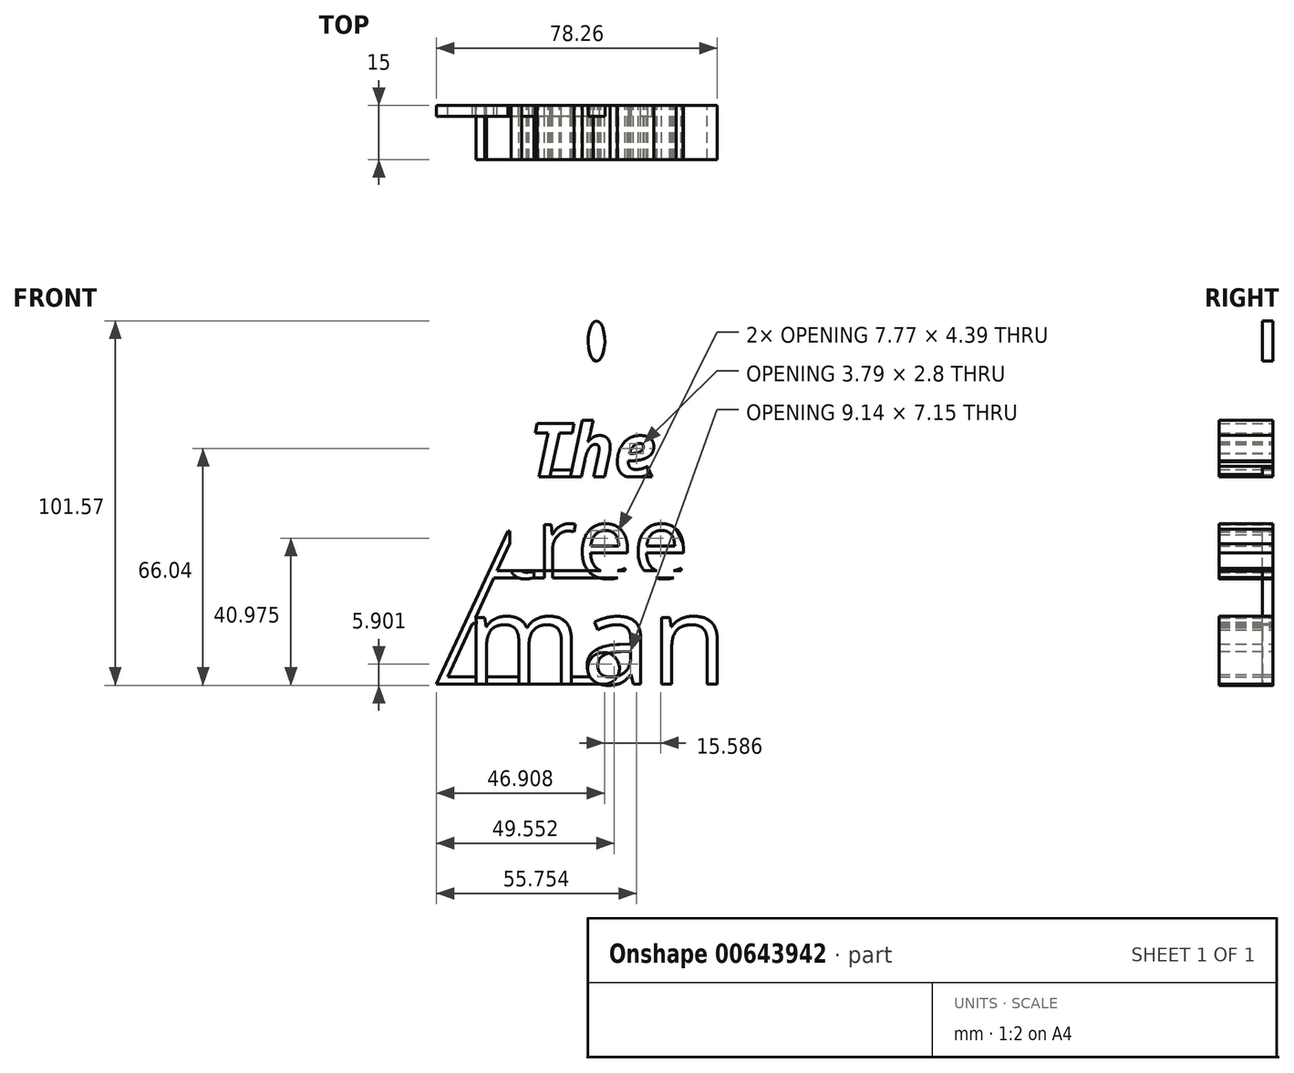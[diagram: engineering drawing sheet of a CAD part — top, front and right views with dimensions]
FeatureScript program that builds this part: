
annotation { "Feature Type Name" : "Feature", "Feature Type Description" : "" }
export const myFeature = defineFeature(function(context is Context, id is Id, definition is map)
    precondition{}
    {
        {
            var Q0;
            Q0=qCreatedBy(makeId("Front.planeOp"),FACE);
            var sketch = newSketch(context, id + "F0", { "sketchPlane" : qUnion([Q0])});
            skText(sketch, "E0", { "text": "The", "fontName": "OpenSans-BoldItalic.ttf"});
            skText(sketch, "E1", { "text": "tree", "fontName": "OpenSans-Regular.ttf"});
            skText(sketch, "E2", { "text": "man", "fontName": "OpenSans-Regular.ttf"});
            skLineSegment(sketch, "E3", {"start": v(-44.6, -34.27) * mm, "end": v(-24.68, 8.45) * mm});
            skLineSegment(sketch, "E4", {"start": v(0, 61.37) * mm, "end": v(12.27, 35.05) * mm});
            skLineSegment(sketch, "E5", {"start": v(44.6, -34.27) * mm, "end": v(-44.6, -34.27) * mm});
            skLineSegment(sketch, "E6.0", {"start": v(0, 56.63) * mm, "end": v(10.22, 34.73) * mm});
            skLineSegment(sketch, "E6.1", {"start": v(-41.46, -32.27) * mm, "end": v(-34.51, -17.38) * mm});
            skLineSegment(sketch, "E6.2", {"start": v(41.46, -32.27) * mm, "end": v(33.66, -32.27) * mm});
            skLineSegment(sketch, "E7", {"start": v(-14.56, -4.69) * mm, "end": v(-17.56, -4.69) * mm});
            skLineSegment(sketch, "E8", {"start": v(-17.56, -4.69) * mm, "end": v(2.4, -4.69) * mm});
            skLineSegment(sketch, "E9.trimOffspring", {"start": v(-33.72, -15.67) * mm, "end": v(-24.1, 4.94) * mm});
            skPoint(sketch, "E10", {"position": v(-33.48, -32.27) * mm});
            skPoint(sketch, "E11", {"position": v(-30.66, -32.27) * mm});
            skLineSegment(sketch, "E12.trimOffspring", {"start": v(-33.48, -32.27) * mm, "end": v(-41.46, -32.27) * mm});
            skPoint(sketch, "E13", {"position": v(-21.64, -32.27) * mm});
            skPoint(sketch, "E14", {"position": v(-18.84, -32.27) * mm});
            skPoint(sketch, "E15", {"position": v(-9.8, -32.27) * mm});
            skPoint(sketch, "E16", {"position": v(-6.99, -32.27) * mm});
            skPoint(sketch, "E17", {"position": v(-1.74, -32.27) * mm});
            skPoint(sketch, "E18", {"position": v(9.02, -32.27) * mm});
            skPoint(sketch, "E19", {"position": v(9.83, -32.27) * mm});
            skPoint(sketch, "E20", {"position": v(12.33, -32.27) * mm});
            skPoint(sketch, "E21", {"position": v(18.13, -32.27) * mm});
            skPoint(sketch, "E22", {"position": v(20.94, -32.27) * mm});
            skPoint(sketch, "E23", {"position": v(30.85, -32.27) * mm});
            skPoint(sketch, "E24", {"position": v(33.66, -32.27) * mm});
            skLineSegment(sketch, "E25.trimOffspring", {"start": v(30.85, -32.27) * mm, "end": v(20.94, -32.27) * mm});
            skLineSegment(sketch, "E26.trimOffspring", {"start": v(18.13, -32.27) * mm, "end": v(12.33, -32.27) * mm});
            skLineSegment(sketch, "E27.trimOffspring", {"start": v(-1.74, -32.27) * mm, "end": v(-6.99, -32.27) * mm});
            skLineSegment(sketch, "E28.trimOffspring", {"start": v(-9.8, -32.27) * mm, "end": v(-18.84, -32.27) * mm});
            skLineSegment(sketch, "E29.trimOffspring", {"start": v(-21.64, -32.27) * mm, "end": v(-30.66, -32.27) * mm});
            skPoint(sketch, "E30", {"position": v(-22.3, 13.55) * mm});
            skPoint(sketch, "E31", {"position": v(-24.68, 8.45) * mm});
            skPoint(sketch, "E32", {"position": v(-21.67, 10.17) * mm});
            skPoint(sketch, "E33", {"position": v(-24.1, 4.94) * mm});
            skLineSegment(sketch, "E34.trimOffspring", {"start": v(-22.3, 13.55) * mm, "end": v(-14.67, 29.9) * mm});
            skLineSegment(sketch, "E35.trimOffspring", {"start": v(-21.67, 10.17) * mm, "end": v(-15.47, 23.45) * mm});
            skPoint(sketch, "E36", {"position": v(22.24, 8.94) * mm});
            skPoint(sketch, "E37", {"position": v(24.13, 4.89) * mm});
            skLineSegment(sketch, "E38.trimOffspring", {"start": v(24.13, 4.89) * mm, "end": v(41.46, -32.27) * mm});
            skLineSegment(sketch, "E39.bottom", {"start": v(-28.6, -4.69) * mm, "end": v(28.6, -4.69) * mm});
            skLineSegment(sketch, "E39.top", {"start": v(-27.66, -2.69) * mm, "end": v(-23.74, -2.69) * mm});
            skPoint(sketch, "E40", {"position": v(21.5, -4.69) * mm});
            skPoint(sketch, "E41", {"position": v(21.45, -2.69) * mm});
            skPoint(sketch, "E42", {"position": v(23.56, -2.69) * mm});
            skPoint(sketch, "E43", {"position": v(16.55, -4.69) * mm});
            skPoint(sketch, "E44", {"position": v(16.9, -2.69) * mm});
            skPoint(sketch, "E45", {"position": v(13.31, -2.69) * mm});
            skPoint(sketch, "E46", {"position": v(7.98, -2.69) * mm});
            skPoint(sketch, "E47", {"position": v(5.84, -2.69) * mm});
            skPoint(sketch, "E48", {"position": v(5.92, -4.69) * mm});
            skPoint(sketch, "E49", {"position": v(1.3, -2.69) * mm});
            skPoint(sketch, "E50", {"position": v(-2.28, -2.69) * mm});
            skPoint(sketch, "E51", {"position": v(0.95, -4.69) * mm});
            skPoint(sketch, "E52", {"position": v(-12.23, -2.69) * mm});
            skPoint(sketch, "E53", {"position": v(-14.48, -2.69) * mm});
            skPoint(sketch, "E54", {"position": v(-14.47, -4.69) * mm});
            skPoint(sketch, "E55", {"position": v(-12.23, -4.69) * mm});
            skPoint(sketch, "E56", {"position": v(-17.8, -4.69) * mm});
            skPoint(sketch, "E57", {"position": v(-21.63, -4.69) * mm});
            skPoint(sketch, "E58", {"position": v(-20.88, -2.69) * mm});
            skPoint(sketch, "E59", {"position": v(-23.74, -2.69) * mm});
            skLineSegment(sketch, "E60.trimOffspring", {"start": v(-20.88, -2.69) * mm, "end": v(-14.48, -2.69) * mm});
            skLineSegment(sketch, "E61.trimOffspring", {"start": v(-12.23, -2.69) * mm, "end": v(-2.28, -2.69) * mm});
            skLineSegment(sketch, "E62.trimOffspring", {"start": v(7.98, -2.69) * mm, "end": v(13.31, -2.69) * mm});
            skLineSegment(sketch, "E63.trimOffspring", {"start": v(23.56, -2.69) * mm, "end": v(27.66, -2.69) * mm});
            skPoint(sketch, "E64", {"position": v(-10.74, 38.33) * mm});
            skPoint(sketch, "E65", {"position": v(-8.54, 38.33) * mm});
            skPoint(sketch, "E66", {"position": v(-9.76, 35.71) * mm});
            skPoint(sketch, "E67", {"position": v(-10.83, 33.4) * mm});
            skPoint(sketch, "E68", {"position": v(-14.67, 29.9) * mm});
            skPoint(sketch, "E69", {"position": v(-15.47, 23.45) * mm});
            skLineSegment(sketch, "E70.trimOffspring", {"start": v(-10.83, 33.4) * mm, "end": v(-9.76, 35.71) * mm});
            skLineSegment(sketch, "E71.trimOffspring", {"start": v(-10.74, 38.33) * mm, "end": v(0, 61.37) * mm});
            skLineSegment(sketch, "E72.trimOffspring", {"start": v(-8.54, 38.33) * mm, "end": v(0, 56.63) * mm});
            skLineSegment(sketch, "E73.bottom", {"start": v(-17.09, 23.45) * mm, "end": v(16.7, 23.45) * mm});
            skPoint(sketch, "E74", {"position": v(-15.63, 25.45) * mm});
            skPoint(sketch, "E75", {"position": v(-16.03, 23.45) * mm});
            skPoint(sketch, "E76", {"position": v(-17.09, 24.72) * mm});
            skPoint(sketch, "E77", {"position": v(-16.75, 25.45) * mm});
            skPoint(sketch, "E78", {"position": v(-12.53, 25.45) * mm});
            skPoint(sketch, "E79", {"position": v(-12.92, 23.45) * mm});
            skPoint(sketch, "E80", {"position": v(-6.86, 25.45) * mm});
            skPoint(sketch, "E81", {"position": v(-7.3, 23.45) * mm});
            skPoint(sketch, "E82", {"position": v(-3.82, 25.45) * mm});
            skPoint(sketch, "E83", {"position": v(-0.38, 25.45) * mm});
            skPoint(sketch, "E84", {"position": v(2.68, 25.45) * mm});
            skPoint(sketch, "E85", {"position": v(6.24, 25.45) * mm});
            skPoint(sketch, "E86", {"position": v(8.74, 23.45) * mm});
            skPoint(sketch, "E87", {"position": v(12.34, 23.45) * mm});
            skPoint(sketch, "E88", {"position": v(14.25, 25.45) * mm});
            skPoint(sketch, "E89", {"position": v(14.25, 26.08) * mm});
            skPoint(sketch, "E90", {"position": v(14.12, 26.35) * mm});
            skPoint(sketch, "E91", {"position": v(13.14, 28.46) * mm});
            skPoint(sketch, "E92", {"position": v(14.88, 29.45) * mm});
            skPoint(sketch, "E93", {"position": v(12.17, 30.54) * mm});
            skPoint(sketch, "E94", {"position": v(11.12, 32.79) * mm});
            skPoint(sketch, "E95", {"position": v(10.22, 34.73) * mm});
            skPoint(sketch, "E96", {"position": v(12.27, 35.05) * mm});
            skLineSegment(sketch, "E97.trimOffspring", {"start": v(11.12, 32.79) * mm, "end": v(12.17, 30.54) * mm});
            skLineSegment(sketch, "E98.trimOffspring", {"start": v(14.88, 29.45) * mm, "end": v(44.6, -34.27) * mm});
            skLineSegment(sketch, "E99.trimOffspring", {"start": v(13.14, 28.46) * mm, "end": v(14.12, 26.35) * mm});
            skLineSegment(sketch, "E100.trimOffspring", {"start": v(-12.53, 25.45) * mm, "end": v(-6.86, 25.45) * mm});
            skLineSegment(sketch, "E101.trimOffspring", {"start": v(-3.82, 25.45) * mm, "end": v(-0.38, 25.45) * mm});
            skLineSegment(sketch, "E102.trimOffspring", {"start": v(2.68, 25.45) * mm, "end": v(6.24, 25.45) * mm});
            skLineSegment(sketch, "E103.trimOffspring", {"start": v(14.25, 26.08) * mm, "end": v(22.24, 8.94) * mm});
            skPoint(sketch, "E104.orphan", {"position": v(-29.52, -4.69) * mm});
            skLineSegment(sketch, "E105", {"start": v(-44.6, -34.27) * mm, "end": v(44.6, -34.27) * mm});
            skPoint(sketch, "E106", {"position": v(1.02, -34.27) * mm});
            skPoint(sketch, "E107", {"position": v(6.1, -34.27) * mm});
            skLineSegment(sketch, "E108", {"start": v(-33.47, -15.7) * mm, "end": v(-33.47, -15.82) * mm});
            skLineSegment(sketch, "E109", {"start": v(-33.72, -15.67) * mm, "end": v(-33.47, -15.7) * mm});
            skLineSegment(sketch, "E110", {"start": v(-34.51, -17.38) * mm, "end": v(-33.38, -17.38) * mm});
            skLineSegment(sketch, "E111", {"start": v(-33.38, -17.38) * mm, "end": v(-33.47, -15.82) * mm});
            skLineSegment(sketch, "E112", {"start": v(-33.49, -32.27) * mm, "end": v(-33.46, -32.27) * mm});
            skLineSegment(sketch, "E113", {"start": v(-25.1, -2.69) * mm, "end": v(-9.87, -2.69) * mm});
            skLineSegment(sketch, "E114", {"start": v(-9.87, -2.69) * mm, "end": v(28.26, -2.69) * mm});
            skLineSegment(sketch, "E115", {"start": v(21.51, 10.5) * mm, "end": v(22.72, 7.91) * mm});
            skLineSegment(sketch, "E116", {"start": v(22.72, 7.91) * mm, "end": v(24.6, 3.9) * mm});
            skLineSegment(sketch, "E117", {"start": v(-21.47, 10.59) * mm, "end": v(-21.99, 9.48) * mm});
            skLineSegment(sketch, "E118", {"start": v(-21.99, 14.22) * mm, "end": v(-22.68, 12.72) * mm});
            skLineSegment(sketch, "E119", {"start": v(-24.9, 7.98) * mm, "end": v(-24.34, 9.17) * mm});
            skLineSegment(sketch, "E120", {"start": v(-24.6, 3.89) * mm, "end": v(-23.63, 5.96) * mm});
            skLineSegment(sketch, "E121", {"start": v(-31.5, -32.27) * mm, "end": v(-20.68, -32.27) * mm});
            skLineSegment(sketch, "E122", {"start": v(-19.42, -32.27) * mm, "end": v(-9.2, -32.27) * mm});
            skLineSegment(sketch, "E123", {"start": v(-7.56, -32.27) * mm, "end": v(-1.13, -32.27) * mm});
            skLineSegment(sketch, "E124", {"start": v(8.52, -32.27) * mm, "end": v(10.35, -32.27) * mm});
            skLineSegment(sketch, "E125", {"start": v(11.87, -32.27) * mm, "end": v(18.74, -32.27) * mm});
            skLineSegment(sketch, "E126", {"start": v(-35.1, -32.27) * mm, "end": v(-32.68, -32.27) * mm});
            skLineSegment(sketch, "E127", {"start": v(-7.64, 40.25) * mm, "end": v(-8.95, 37.44) * mm});
            skLineSegment(sketch, "E128", {"start": v(-9.2, 41.63) * mm, "end": v(-11.35, 37.04) * mm});
            skLineSegment(sketch, "E129", {"start": v(7.66, 40.21) * mm, "end": v(10.61, 33.87) * mm});
            skLineSegment(sketch, "E130", {"start": v(11.6, 36.48) * mm, "end": v(13.05, 33.37) * mm});
            skLineSegment(sketch, "E131", {"start": v(11.94, 31.02) * mm, "end": v(12.47, 29.9) * mm});
            skLineSegment(sketch, "E132", {"start": v(11.42, 32.14) * mm, "end": v(10.85, 33.37) * mm});
            skLineSegment(sketch, "E133", {"start": v(13.98, 26.66) * mm, "end": v(14.16, 26.27) * mm});
            skLineSegment(sketch, "E134", {"start": v(14.21, 26.17) * mm, "end": v(14.32, 25.92) * mm});
            skLineSegment(sketch, "E135", {"start": v(26.76, -4.69) * mm, "end": v(29.38, -4.69) * mm});
            skLineSegment(sketch, "E136", {"start": v(34.91, -32.27) * mm, "end": v(32.73, -32.27) * mm});
            skLineSegment(sketch, "E137", {"start": v(29.2, -32.27) * mm, "end": v(31.82, -32.27) * mm});
            skLineSegment(sketch, "E138", {"start": v(22, -32.27) * mm, "end": v(19.96, -32.27) * mm});
            skLineSegment(sketch, "E139", {"start": v(-3.25, 25.45) * mm, "end": v(-4.75, 25.45) * mm});
            skLineSegment(sketch, "E140", {"start": v(-4.75, 25.45) * mm, "end": v(0.66, 25.45) * mm});
            skLineSegment(sketch, "E141", {"start": v(1.69, 25.45) * mm, "end": v(6.86, 25.45) * mm});
            skLineSegment(sketch, "E142", {"start": v(13.43, 27.84) * mm, "end": v(12.94, 28.88) * mm});
            skLineSegment(sketch, "E143", {"start": v(-8.5, -34.27) * mm, "end": v(-8.5, -51.14) * mm});
            skLineSegment(sketch, "E144", {"start": v(-8.5, -51.14) * mm, "end": v(-10.79, -56.05) * mm});
            skLineSegment(sketch, "E145", {"start": v(-10.79, -56.05) * mm, "end": v(0, -56.05) * mm});
            skLineSegment(sketch, "E146.MirrorCS", {"start": v(8.5, -34.27) * mm, "end": v(8.5, -51.14) * mm});
            skLineSegment(sketch, "E147.MirrorCS", {"start": v(8.5, -51.14) * mm, "end": v(10.79, -56.05) * mm});
            skLineSegment(sketch, "E148.MirrorCS", {"start": v(10.79, -56.05) * mm, "end": v(0, -56.05) * mm});
            skLineSegment(sketch, "E149.0", {"start": v(5.5, -34.27) * mm, "end": v(5.5, -53.05) * mm});
            skLineSegment(sketch, "E149.1", {"start": v(5.5, -53.05) * mm, "end": v(0, -53.05) * mm});
            skLineSegment(sketch, "E149.2", {"start": v(-5.5, -53.05) * mm, "end": v(0, -53.05) * mm});
            skLineSegment(sketch, "E149.3", {"start": v(-5.5, -34.27) * mm, "end": v(-5.5, -53.05) * mm});
            const initialGuessF0  = {"E0": [-0.01874, 0.02345, 1, 0, 0.015], "E1": [-0.02667, -0.00469, 1, 0, 0.02], "E2": [-0.03646, -0.03427, 1, 0, 0.025]};
            skSetInitialGuess(sketch, initialGuessF0);
            skSolve(sketch);
        }
        {
            var Q0;
            {var subQ5=sQuery(id+"F0.wireOp",EDGE,"E114");var subQ12=makeQuery(id+"F0.imprint","IMPRINT",VERTEX,{"disambiguationData":[OD(3.0)],"derivedFrom":subQ5});Q0=makeQuery(id+"F0.imprint","IMPRINT",FACE,{"disambiguationData":[TD([[makeQuery(id+"F0.imprint","IMPRINT",EDGE,{"disambiguationData":[TD([[subQ12,1.0]])],"derivedFrom":subQ5}),-1.0]])]});}
            var Q1;
            {var subQ3=sQuery(id+"F0.wireOp",EDGE,"E114");var subQ12=makeQuery(id+"F0.imprint","IMPRINT",VERTEX,{"disambiguationData":[OD(1.0)],"derivedFrom":subQ3});Q1=makeQuery(id+"F0.imprint","IMPRINT",FACE,{"disambiguationData":[TD([[makeQuery(id+"F0.imprint","IMPRINT",EDGE,{"disambiguationData":[TD([[subQ12,1.0]])],"derivedFrom":subQ3}),-1.0]])]});}
            var Q2;
            {var subQ0=sQuery(id+"F0.wireOp",EDGE,"E105");var subQ1=sQuery(id+"F0.wireOp",EDGE,"E2.sketch_text.stroke-45");var subQ2=makeQuery(id+"F0.imprint","INTERSECT",VERTEX,{"derivedFrom":[subQ1,subQ0]});Q2=makeQuery(id+"F0.imprint","IMPRINT",FACE,{"disambiguationData":[TD([[makeQuery(id+"F0.imprint","IMPRINT",EDGE,{"disambiguationData":[TD([[subQ2,1.0]])],"derivedFrom":subQ1}),1.0]])]});}
            var Q3;
            {var subQ5=sQuery(id+"F0.wireOp",EDGE,"E25.trimOffspring");Q3=makeQuery(id+"F0.imprint","IMPRINT",FACE,{"disambiguationData":[TD([[makeQuery(id+"F0.imprint","IMPRINT",EDGE,{"derivedFrom":subQ5}),1.0]])]});}
            var Q4;
            {var subQ0=sQuery(id+"F0.wireOp",EDGE,"E105");var subQ1=sQuery(id+"F0.wireOp",EDGE,"E2.sketch_text.stroke-28");var subQ2=makeQuery(id+"F0.imprint","INTERSECT",VERTEX,{"derivedFrom":[subQ1,subQ0]});Q4=makeQuery(id+"F0.imprint","IMPRINT",FACE,{"disambiguationData":[TD([[makeQuery(id+"F0.imprint","IMPRINT",EDGE,{"disambiguationData":[TD([[subQ2,-1.0]])],"derivedFrom":subQ1}),1.0]])]});}
            var Q5;
            {var subQ0=sQuery(id+"F0.wireOp",EDGE,"E105");var subQ1=sQuery(id+"F0.wireOp",EDGE,"E2.sketch_text.stroke-26");var subQ2=makeQuery(id+"F0.imprint","INTERSECT",VERTEX,{"derivedFrom":[subQ1,subQ0]});Q5=makeQuery(id+"F0.imprint","IMPRINT",FACE,{"disambiguationData":[TD([[makeQuery(id+"F0.imprint","IMPRINT",EDGE,{"disambiguationData":[TD([[subQ2,1.0]])],"derivedFrom":subQ1}),1.0]])]});}
            var Q6;
            {var subQ0=sQuery(id+"F0.wireOp",EDGE,"E105");var subQ1=sQuery(id+"F0.wireOp",EDGE,"E2.sketch_text.stroke-0");var subQ2=makeQuery(id+"F0.imprint","INTERSECT",VERTEX,{"derivedFrom":[subQ1,subQ0]});Q6=makeQuery(id+"F0.imprint","IMPRINT",FACE,{"disambiguationData":[TD([[makeQuery(id+"F0.imprint","IMPRINT",EDGE,{"disambiguationData":[TD([[subQ2,-1.0]])],"derivedFrom":subQ1}),1.0]])]});}
            var Q7;
            {var subQ0=sQuery(id+"F0.wireOp",EDGE,"E121");var subQ1=makeQuery(id+"F0.imprint","IMPRINT",VERTEX,{"derivedFrom":subQ0});Q7=makeQuery(id+"F0.imprint","IMPRINT",FACE,{"disambiguationData":[TD([[makeQuery(id+"F0.imprint","IMPRINT",EDGE,{"disambiguationData":[TD([[subQ1,1.0]])],"derivedFrom":subQ0}),-1.0]])]});}
            var Q8;
            {var subQ17=sQuery(id+"F0.wireOp",EDGE,"E3");Q8=makeQuery(id+"F0.imprint","IMPRINT",FACE,{"disambiguationData":[TD([[makeQuery(id+"F0.imprint","IMPRINT",EDGE,{"derivedFrom":subQ17}),-1.0]])]});}
            var Q9;
            {var subQ0=sQuery(id+"F0.wireOp",EDGE,"E39.top");Q9=makeQuery(id+"F0.imprint","IMPRINT",FACE,{"disambiguationData":[TD([[makeQuery(id+"F0.imprint","IMPRINT",EDGE,{"derivedFrom":subQ0}),-1.0]])]});}
            var Q10;
            {var subQ12=sQuery(id+"F0.wireOp",EDGE,"E1.sketch_text.stroke-0");Q10=makeQuery(id+"F0.imprint","IMPRINT",FACE,{"disambiguationData":[TD([[makeQuery(id+"F0.imprint","IMPRINT",EDGE,{"derivedFrom":subQ12}),1.0]])]});}
            var Q11;
            {var subQ3=sQuery(id+"F0.wireOp",EDGE,"E39.bottom");var subQ8=sQuery(id+"F0.wireOp",EDGE,"E1.sketch_text.stroke-24");var subQ10=makeQuery(id+"F0.imprint","INTERSECT",VERTEX,{"derivedFrom":[subQ8,subQ3]});Q11=makeQuery(id+"F0.imprint","IMPRINT",FACE,{"disambiguationData":[TD([[makeQuery(id+"F0.imprint","IMPRINT",EDGE,{"disambiguationData":[TD([[subQ10,1.0]])],"derivedFrom":subQ8}),1.0]])]});}
            var Q12;
            {var subQ1=sQuery(id+"F0.wireOp",EDGE,"E1.sketch_text.stroke-12");Q12=makeQuery(id+"F0.imprint","IMPRINT",FACE,{"disambiguationData":[TD([[makeQuery(id+"F0.imprint","IMPRINT",EDGE,{"derivedFrom":subQ1}),1.0]])]});}
            var Q13;
            {var subQ15=sQuery(id+"F0.wireOp",EDGE,"E4");Q13=makeQuery(id+"F0.imprint","IMPRINT",FACE,{"disambiguationData":[TD([[makeQuery(id+"F0.imprint","IMPRINT",EDGE,{"derivedFrom":subQ15}),-1.0]])]});}
            var Q14;
            {var subQ0=sQuery(id+"F0.wireOp",EDGE,"E73.bottom");var subQ1=sQuery(id+"F0.wireOp",EDGE,"E0.sketch_text.stroke-7");var subQ2=makeQuery(id+"F0.imprint","INTERSECT",VERTEX,{"derivedFrom":[subQ1,subQ0]});Q14=makeQuery(id+"F0.imprint","IMPRINT",FACE,{"disambiguationData":[TD([[makeQuery(id+"F0.imprint","IMPRINT",EDGE,{"disambiguationData":[TD([[subQ2,1.0]])],"derivedFrom":subQ1}),1.0]])]});}
            var Q15;
            {var subQ0=sQuery(id+"F0.wireOp",EDGE,"E140");var subQ1=makeQuery(id+"F0.imprint","IMPRINT",VERTEX,{"disambiguationData":[OD(0.0)],"derivedFrom":subQ0});Q15=makeQuery(id+"F0.imprint","IMPRINT",FACE,{"disambiguationData":[TD([[makeQuery(id+"F0.imprint","IMPRINT",EDGE,{"disambiguationData":[TD([[subQ1,-1.0]])],"derivedFrom":subQ0}),-1.0]])]});}
            var Q16;
            {var subQ5=sQuery(id+"F0.wireOp",EDGE,"E141");var subQ6=makeQuery(id+"F0.imprint","IMPRINT",VERTEX,{"disambiguationData":[OD(0.0)],"derivedFrom":subQ5});Q16=makeQuery(id+"F0.imprint","IMPRINT",FACE,{"disambiguationData":[TD([[makeQuery(id+"F0.imprint","IMPRINT",EDGE,{"disambiguationData":[TD([[subQ6,-1.0]])],"derivedFrom":subQ5}),-1.0]])]});}
            var Q17;
            {var subQ1=sQuery(id+"F0.wireOp",EDGE,"E6.2");Q17=makeQuery(id+"F0.imprint","IMPRINT",FACE,{"disambiguationData":[TD([[makeQuery(id+"F0.imprint","IMPRINT",EDGE,{"derivedFrom":subQ1}),1.0]])]});}
            var Q18;
            {var subQ2=sQuery(id+"F0.wireOp",EDGE,"E0.sketch_text.stroke-49");var subQ6=sQuery(id+"F0.wireOp",EDGE,"E0.sketch_text.stroke-50");var subQ8=makeQuery(id+"F0.imprint","INTERSECT",VERTEX,{"derivedFrom":[subQ2,subQ6]});Q18=makeQuery(id+"F0.imprint","IMPRINT",FACE,{"disambiguationData":[TD([[makeQuery(id+"F0.imprint","IMPRINT",EDGE,{"disambiguationData":[TD([[subQ8,1.0]])],"derivedFrom":subQ2}),1.0]])]});}
            extrude(context, id + "F1", {"entities" : qUnion([Q0, Q1, Q2, Q3, Q4, Q5, Q6, Q7, Q8, Q9, Q10, Q11, Q12, Q13, Q14, Q15, Q16, Q17, Q18]), "depth" : 3 * mm, "offsetDistance" : 25 * mm});
        }
        {
            var Q0;
            {var subQ14=sQuery(id+"F0.wireOp",EDGE,"E0.sketch_text.stroke-2");Q0=makeQuery(id+"F0.imprint","IMPRINT",FACE,{"disambiguationData":[TD([[makeQuery(id+"F0.imprint","IMPRINT",EDGE,{"derivedFrom":subQ14}),-1.0]])]});}
            var Q1;
            {var subQ10=sQuery(id+"F0.wireOp",EDGE,"E0.sketch_text.stroke-10");Q1=makeQuery(id+"F0.imprint","IMPRINT",FACE,{"disambiguationData":[TD([[makeQuery(id+"F0.imprint","IMPRINT",EDGE,{"derivedFrom":subQ10}),-1.0]])]});}
            var Q2;
            {var subQ21=sQuery(id+"F0.wireOp",EDGE,"E0.sketch_text.stroke-28");Q2=makeQuery(id+"F0.imprint","IMPRINT",FACE,{"disambiguationData":[TD([[makeQuery(id+"F0.imprint","IMPRINT",EDGE,{"derivedFrom":subQ21}),-1.0]])]});}
            var Q3;
            {var subQ10=sQuery(id+"F0.wireOp",EDGE,"E1.sketch_text.stroke-8");Q3=makeQuery(id+"F0.imprint","IMPRINT",FACE,{"disambiguationData":[TD([[makeQuery(id+"F0.imprint","IMPRINT",EDGE,{"derivedFrom":subQ10}),-1.0]])]});}
            var Q4;
            {var subQ8=sQuery(id+"F0.wireOp",EDGE,"E1.sketch_text.stroke-0");Q4=makeQuery(id+"F0.imprint","IMPRINT",FACE,{"disambiguationData":[TD([[makeQuery(id+"F0.imprint","IMPRINT",EDGE,{"derivedFrom":subQ8}),-1.0]])]});}
            var Q5;
            Q5=makeQuery(id+"F0.imprint","IMPRINT",FACE,{"disambiguationData":[TD([[makeQuery(id+"F0.imprint","IMPRINT",EDGE,{"derivedFrom":sQuery(id+"F0.wireOp",EDGE,"E1.sketch_text.stroke-19")}),-1.0]])]});
            var Q6;
            {var subQ0=sQuery(id+"F0.wireOp",EDGE,"E113");var subQ1=makeQuery(id+"F0.imprint","IMPRINT",VERTEX,{"disambiguationData":[OD(3.0)],"derivedFrom":subQ0});Q6=makeQuery(id+"F0.imprint","IMPRINT",FACE,{"disambiguationData":[TD([[makeQuery(id+"F0.imprint","IMPRINT",EDGE,{"disambiguationData":[TD([[subQ1,1.0]])],"derivedFrom":subQ0}),-1.0]])]});}
            var Q7;
            {var subQ5=sQuery(id+"F0.wireOp",EDGE,"E1.sketch_text.stroke-34");Q7=makeQuery(id+"F0.imprint","IMPRINT",FACE,{"disambiguationData":[TD([[makeQuery(id+"F0.imprint","IMPRINT",EDGE,{"derivedFrom":subQ5}),-1.0]])]});}
            var Q8;
            {var subQ4=sQuery(id+"F0.wireOp",EDGE,"E39.bottom");var subQ5=makeQuery(id+"F0.imprint","IMPRINT",VERTEX,{"disambiguationData":[OD(2.0)],"derivedFrom":subQ4});Q8=makeQuery(id+"F0.imprint","IMPRINT",FACE,{"disambiguationData":[TD([[makeQuery(id+"F0.imprint","IMPRINT",EDGE,{"disambiguationData":[TD([[subQ5,1.0]])],"derivedFrom":subQ4}),1.0]])]});}
            var Q9;
            {var subQ3=sQuery(id+"F0.wireOp",EDGE,"E114");var subQ17=makeQuery(id+"F0.imprint","IMPRINT",VERTEX,{"disambiguationData":[OD(2.0)],"derivedFrom":subQ3});Q9=makeQuery(id+"F0.imprint","IMPRINT",FACE,{"disambiguationData":[TD([[makeQuery(id+"F0.imprint","IMPRINT",EDGE,{"disambiguationData":[TD([[subQ17,1.0]])],"derivedFrom":subQ3}),-1.0]])]});}
            var Q10;
            {var subQ11=sQuery(id+"F0.wireOp",EDGE,"E1.sketch_text.stroke-53");Q10=makeQuery(id+"F0.imprint","IMPRINT",FACE,{"disambiguationData":[TD([[makeQuery(id+"F0.imprint","IMPRINT",EDGE,{"derivedFrom":subQ11}),-1.0]])]});}
            var Q11;
            {var subQ0=sQuery(id+"F0.wireOp",EDGE,"E1.sketch_text.stroke-64");Q11=makeQuery(id+"F0.imprint","IMPRINT",FACE,{"disambiguationData":[TD([[makeQuery(id+"F0.imprint","IMPRINT",EDGE,{"derivedFrom":subQ0}),-1.0]])]});}
            var Q12;
            {var subQ0=sQuery(id+"F0.wireOp",EDGE,"E1.sketch_text.stroke-45");Q12=makeQuery(id+"F0.imprint","IMPRINT",FACE,{"disambiguationData":[TD([[makeQuery(id+"F0.imprint","IMPRINT",EDGE,{"derivedFrom":subQ0}),-1.0]])]});}
            var Q13;
            {var subQ0=sQuery(id+"F0.wireOp",EDGE,"E1.sketch_text.stroke-43");var subQ1=sQuery(id+"F0.wireOp",EDGE,"E1.sketch_text.stroke-42");var subQ2=makeQuery(id+"F0.imprint","INTERSECT",VERTEX,{"derivedFrom":[subQ1,subQ0]});Q13=makeQuery(id+"F0.imprint","IMPRINT",FACE,{"disambiguationData":[TD([[makeQuery(id+"F0.imprint","IMPRINT",EDGE,{"disambiguationData":[TD([[subQ2,1.0]])],"derivedFrom":subQ1}),-1.0]])]});}
            var Q14;
            {var subQ0=sQuery(id+"F0.wireOp",EDGE,"E1.sketch_text.stroke-62");var subQ1=sQuery(id+"F0.wireOp",EDGE,"E1.sketch_text.stroke-61");var subQ2=makeQuery(id+"F0.imprint","INTERSECT",VERTEX,{"derivedFrom":[subQ1,subQ0]});Q14=makeQuery(id+"F0.imprint","IMPRINT",FACE,{"disambiguationData":[TD([[makeQuery(id+"F0.imprint","IMPRINT",EDGE,{"disambiguationData":[TD([[subQ2,1.0]])],"derivedFrom":subQ1}),-1.0]])]});}
            var Q15;
            {var subQ0=sQuery(id+"F0.wireOp",EDGE,"E1.sketch_text.stroke-4");Q15=makeQuery(id+"F0.imprint","IMPRINT",FACE,{"disambiguationData":[TD([[makeQuery(id+"F0.imprint","IMPRINT",EDGE,{"derivedFrom":subQ0}),-1.0]])]});}
            var Q16;
            {var subQ16=sQuery(id+"F0.wireOp",EDGE,"E2.sketch_text.stroke-1");Q16=makeQuery(id+"F0.imprint","IMPRINT",FACE,{"disambiguationData":[TD([[makeQuery(id+"F0.imprint","IMPRINT",EDGE,{"derivedFrom":subQ16}),-1.0]])]});}
            var Q17;
            {var subQ8=sQuery(id+"F0.wireOp",EDGE,"E2.sketch_text.stroke-29");Q17=makeQuery(id+"F0.imprint","IMPRINT",FACE,{"disambiguationData":[TD([[makeQuery(id+"F0.imprint","IMPRINT",EDGE,{"derivedFrom":subQ8}),-1.0]])]});}
            var Q18;
            {var subQ0=sQuery(id+"F0.wireOp",EDGE,"E2.sketch_text.stroke-32");var subQ1=sQuery(id+"F0.wireOp",EDGE,"E2.sketch_text.stroke-31");var subQ2=makeQuery(id+"F0.imprint","INTERSECT",VERTEX,{"derivedFrom":[subQ1,subQ0]});Q18=makeQuery(id+"F0.imprint","IMPRINT",FACE,{"disambiguationData":[TD([[makeQuery(id+"F0.imprint","IMPRINT",EDGE,{"disambiguationData":[TD([[subQ2,1.0]])],"derivedFrom":subQ1}),-1.0]])]});}
            var Q19;
            {var subQ14=sQuery(id+"F0.wireOp",EDGE,"E2.sketch_text.stroke-56");Q19=makeQuery(id+"F0.imprint","IMPRINT",FACE,{"disambiguationData":[TD([[makeQuery(id+"F0.imprint","IMPRINT",EDGE,{"derivedFrom":subQ14}),-1.0]])]});}
            extrude(context, id + "F2", {"entities" : qUnion([Q0, Q1, Q2, Q3, Q4, Q5, Q6, Q7, Q8, Q9, Q10, Q11, Q12, Q13, Q14, Q15, Q16, Q17, Q18, Q19]), "depth" : 15 * mm, "offsetDistance" : 25 * mm});
        }
        {
            var Q0;
            {var subQ0=sQuery(id+"F0.wireOp",EDGE,"E111");Q0=makeQuery(id+"F0.imprint","IMPRINT",FACE,{"disambiguationData":[TD([[makeQuery(id+"F0.imprint","IMPRINT",EDGE,{"derivedFrom":subQ0}),1.0]])]});}
            extrude(context, id + "F3", {"entities" : qUnion([Q0]), "depth" : 15 * mm, "offsetDistance" : 25 * mm});
        }
        {
            var Q0;
            {var subQ0=sQuery(id+"F0.wireOp",EDGE,"E115");var subQ1=makeQuery(id+"F0.imprint","IMPRINT",VERTEX,{"derivedFrom":subQ0});Q0=makeQuery(id+"F0.imprint","IMPRINT",FACE,{"disambiguationData":[TD([[makeQuery(id+"F0.imprint","IMPRINT",EDGE,{"disambiguationData":[TD([[subQ1,1.0]])],"derivedFrom":subQ0}),1.0]])]});}
            extrude(context, id + "F4", {"entities" : qUnion([Q0]), "depth" : 15 * mm, "offsetDistance" : 25 * mm});
        }
        {
            var Q0;
            Q0=qCreatedBy(makeId("Front.planeOp"),FACE);
            var sketch = newSketch(context, id + "F5", { "sketchPlane" : qUnion([Q0])});
            skEllipse(sketch, "E150", {"center": v(0, 61.36) * mm, "majorRadius": 5.6 * mm, "minorRadius": 2.34 * mm, "majorAxis": v(0, 1)});
            skFitSpline(sketch, "E151.0", {"points": [v(0.94, 69.88) * mm, v(0, 70) * mm, v(-0.94, 69.88) * mm, v(-1.77, 69.58) * mm, v(-2.46, 69.16) * mm, v(-3.02, 68.67) * mm, v(-3.48, 68.15) * mm, v(-3.98, 67.42) * mm, v(-4.45, 66.49) * mm, v(-4.86, 65.29) * mm, v(-5.14, 64.02) * mm, v(-5.3, 62.7) * mm, v(-5.36, 61.36) * mm, v(-5.3, 60) * mm, v(-5.14, 58.7) * mm, v(-4.86, 57.42) * mm, v(-4.45, 56.22) * mm, v(-3.98, 55.29) * mm, v(-3.48, 54.56) * mm, v(-3.02, 54.04) * mm, v(-2.46, 53.55) * mm, v(-1.77, 53.13) * mm, v(-0.94, 52.83) * mm, v(0, 52.71) * mm, v(0.94, 52.83) * mm, v(1.77, 53.13) * mm, v(2.46, 53.55) * mm, v(3.02, 54.04) * mm, v(3.48, 54.56) * mm, v(3.98, 55.29) * mm, v(4.45, 56.22) * mm, v(4.86, 57.42) * mm, v(5.14, 58.7) * mm, v(5.3, 60) * mm, v(5.36, 61.36) * mm, v(5.3, 62.7) * mm, v(5.14, 64.02) * mm, v(4.86, 65.29) * mm, v(4.45, 66.49) * mm, v(3.98, 67.42) * mm, v(3.48, 68.15) * mm, v(3.02, 68.67) * mm, v(2.46, 69.16) * mm, v(1.77, 69.58) * mm, v(0.94, 69.88) * mm, v(0, 70) * mm, v(-0.94, 69.88) * mm, v(0.94, 69.88) * mm]});
            skSolve(sketch);
        }
        {
            var Q0;
            Q0 = qSketchRegion(id + "F5", true);
            extrude(context, id + "F6", {"entities" : qUnion([Q0]), "operationType" : NewBodyOperationType.ADD, "depth" : 3 * mm, "offsetDistance" : 25 * mm});
        }
        {
            var Q0;
            {var subQ7=sQuery(id+"F0.wireOp",EDGE,"E143");Q0=makeQuery(id+"F0.imprint","IMPRINT",FACE,{"disambiguationData":[TD([[makeQuery(id+"F0.imprint","IMPRINT",EDGE,{"derivedFrom":subQ7}),1.0]])]});}
            var Q1;
            {var subQ0=sQuery(id+"F0.wireOp",EDGE,"E105");var subQ1=sQuery(id+"F0.wireOp",EDGE,"E2.sketch_text.stroke-31");var subQ2=makeQuery(id+"F0.imprint","INTERSECT",VERTEX,{"derivedFrom":[subQ1,subQ0]});Q1=makeQuery(id+"F0.imprint","IMPRINT",FACE,{"disambiguationData":[TD([[makeQuery(id+"F0.imprint","IMPRINT",EDGE,{"disambiguationData":[TD([[subQ2,-1.0]])],"derivedFrom":subQ1}),-1.0]])]});}
            extrude(context, id + "F7", {"entities" : qUnion([Q0, Q1]), "depth" : 3 * mm, "offsetDistance" : 25 * mm});
        }
    });
